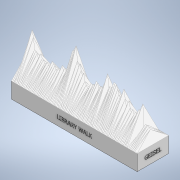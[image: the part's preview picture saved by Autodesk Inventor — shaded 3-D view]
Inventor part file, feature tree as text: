
AUTODESK INVENTOR PART (.ipt)
format: ipt  version: 2020 (Build 240168000, 168)  size: 1,802,752 bytes
history: native  units: in
note: dims shown in document units (in); Inventor stores cm internally (conversion verified against a paired STEP export)
features: extrude x5, sketch x5, projected_geometry x4, other x2
ambient origin geometry x8: Origin, YZ Plane, XZ Plane, XY Plane, X Axis, Y Axis, Z Axis, Center Point
bodies: Solid1 (feature_tree)
feature tree (16):
  other  "test"
  extrude  "Extrusion1"  Depth=2.0in
  extrude  "Extrusion2"  Depth=2.0in
  extrude  "Extrusion3"  Depth=0.32in
  extrude  "Extrusion4"  Depth=0.2in TaperAngle=0.0deg
  extrude  "Extrusion5"  Depth=1.0in
  sketch  "Sketch1"  dims[d0=1.0in d1=0.0in d2=2.0in]
  sketch  "Sketch2"  dims[d3=8.0in d4=2.0in]
  projected_geometry  "Projected Loop1"
  sketch  "Sketch3"  dims[d5=4.0in d6=0.32in]
  projected_geometry  "Projected Loop2"
  sketch  "Sketch4"  dims[d7=0.84in d8=0.2in d9=0.0in]
  projected_geometry  "Projected Loop3"
  sketch  "Sketch5"  dims[d10=8.0in d11=1.0in d12=4.0in d13=0.32in d14=2.0in d15=0.34in d16=0.1in d17=0.0in d18=2.0in d19=1.0in d20=1.0in d21=0.32in d22=0.34in d23=0.5in d24=0.1in d25=0.0in d26=8.0in d27=1.0in d28=4.0in d29=0.32in d30=0.34in d31=2.0in d32=0.1in d33=0.0in]
  projected_geometry  "Projected Loop4"
  other  "MeshFeature1"
